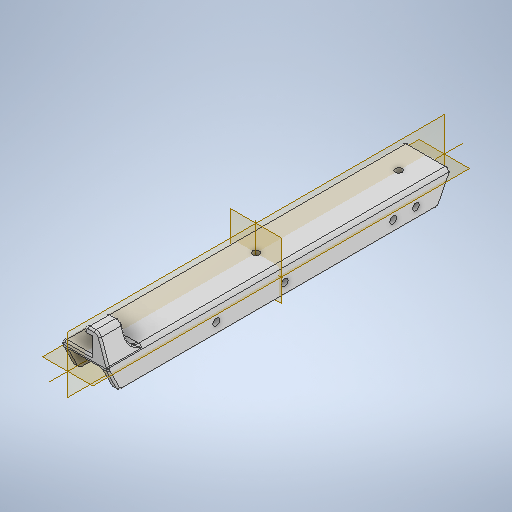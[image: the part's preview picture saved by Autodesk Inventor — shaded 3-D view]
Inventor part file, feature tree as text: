
AUTODESK INVENTOR PART (.ipt)
format: ipt  version: 2025 (Build 290162000, 162)  size: 444,416 bytes
history: native  units: mm
features: fillet x6, sketch x5, hole x3, pattern_linear x3, extrude x2, chamfer x2, projected_geometry x1
ambient origin geometry x8: Origin, YZ Plane, XZ Plane, XY Plane, X Axis, Y Axis, Z Axis, Center Point
bodies: Solid1 (feature_tree)
feature tree (22):
  extrude  "Extrusion1"  Depth=30.2mm
  chamfer  "Chamfer1"  Distance=300.0mm
  chamfer  "Chamfer2"  Distance=10.0mm Angle=60.0deg
  fillet  "Fillet1"  Radius=5.0mm
  hole  "Hole1"  [1 undecoded]
  hole  "Hole2"  [1 undecoded]
  fillet  "Fillet4"  Radius=25.0mm
  pattern_linear  "Rectangular Pattern1"  Count1=2 Spacing1=125.0mm
  pattern_linear  "Rectangular Pattern2"  Spacing1=29.95mm  [1 undecoded]
  extrude  "Extrusion4"  Depth=10.0mm
  fillet  "Fillet5"  Radius=15.2mm
  fillet  "Fillet6"  Radius=7.1mm
  fillet  "Fillet7"  Radius=5.0mm
  fillet  "Fillet8"  Radius=12.0mm
  hole  "Hole3"  [1 undecoded]
  pattern_linear  "Rectangular Pattern3"  Spacing1=3.0mm  [1 undecoded]
  sketch  "Sketch1"  dims[d0=20.0mm d1=30.2mm]
  sketch  "Sketch2"  dims[d2=5.0mm]
  sketch  "Sketch3"  dims[d3=2.0mm]
  sketch  "Sketch8"  dims[d4=3.0mm d5=300.0mm d6=0.0mm d7=20.0mm d8=10.0mm d9=60.0deg]
  projected_geometry  "Projected Loop1"
  sketch  "Sketch9"  dims[d10=20.0mm d11=10.0mm d12=60.0deg d13=5.0mm d14=6.0mm d15=6.0mm d16=4.0mm d17=2.0mm d18=90.0deg d19=8.0mm d20=20.594885mm d21=10.0mm d23=6.0mm d24=6.0mm d25=4.0mm d26=2.0mm d27=90.0deg d28=8.0mm d29=20.594885mm d42=4.0mm d44=25.0mm d45=20.0mm d47=125.0mm d48=29.95mm d49=20.0mm d51=20.0mm d52=15.2mm d53=7.1mm d54=5.0mm d55=12.0mm d56=5.0mm d57=3.0mm d58=0.5mm d59=20.0mm d60=0.0mm d61=10.0mm d62=1.5mm d63=1.5mm d64=0.5mm d65=6.0mm d66=6.0mm d67=4.0mm d68=2.0mm d69=90.0deg d70=8.0mm d71=20.594885mm d72=10.0mm d74=95.0mm d75=20.0mm d77=60.0mm d41=0.0mm d43=0.0mm]
note: 5 required parameter values undecoded (feature->parameter linkage not recoverable at this tier; creation-order binding heuristic only, values carry confidence <= 0.55)
